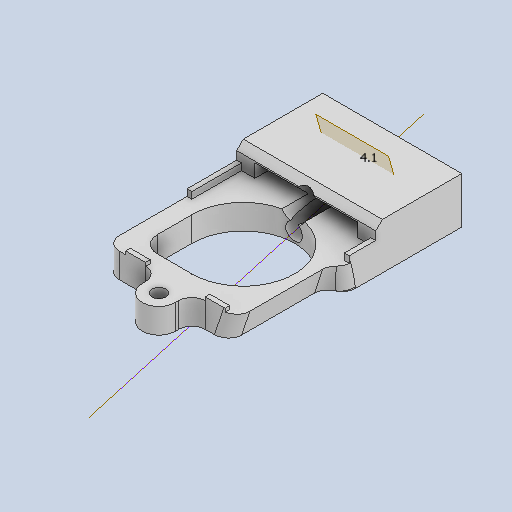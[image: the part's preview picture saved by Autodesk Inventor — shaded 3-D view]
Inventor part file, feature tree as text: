
AUTODESK INVENTOR PART (.ipt)
format: ipt  version: 2023.3 (Build 273359000, 359)  size: 391,168 bytes
history: native  units: mm
features: sketch x15, extrude x9, other x7, hole x5, projected_geometry x5, fillet x3, chamfer x2, plane x2
ambient origin geometry x8: Origin, YZ Plane, XZ Plane, XY Plane, X Axis, Y Axis, Z Axis, Center Point
bodies: Solid1 (feature_tree)
feature tree (48):
  extrude  "Extrusion1"  Depth=14.0mm
  hole  "Hole1"  [1 undecoded]
  extrude  "Extrusion2"  Depth=26.0mm
  hole  "Hole3"  [1 undecoded]
  extrude  "Extrusion3"  Depth=8.0mm TaperAngle=90.0deg
  hole  "Hole2"  [1 undecoded]
  other  "Snap Fit1"
  fillet  "Fillet1"  Radius=2.0mm
  extrude  "Extrusion4"  Depth=8.0mm
  extrude  "Extrusion5"  Depth=2.5mm
  hole  "Hole4"  [1 undecoded]
  fillet  "Fillet2"  Radius=1.0mm
  extrude  "Extrusion6"  Depth=10.0mm
  chamfer  "Chamfer1"  Distance=10.0mm
  chamfer  "Chamfer2"  Distance=4.1mm
  extrude  "Extrusion7"  TaperAngle=45.0deg  [1 undecoded]
  extrude  "Extrusion8"  Depth=10.0mm TaperAngle=0.0deg
  fillet  "Fillet3"  Radius=2.0mm
  sketch  "Sketch15"  dims[d66=18.0mm d68=4.1mm d69=45.0deg d70=31.0mm d71=0.0mm d72=2.0mm d73=2.0mm d74=45.0deg d76=5.0mm d77=6.0mm d78=2.0mm d79=45.0deg d83=15.5mm d84=5.0mm d85=0.0mm d86=0.0mm d87=5.0mm d88=30.0mm d89=0.0mm d90=4.0mm d91=2.5mm d92=45.0deg d93=15.0mm d94=0.0mm d96=1.0mm d97=20.0mm d98=0.0mm d99=4.1mm d100=10.0mm d101=10.0mm d102=5.0mm d103=6.0mm d104=4.0mm d105=2.0mm d106=90.0deg d107=8.0mm d108=0.0mm d67=0.0mm d75=0.5mm d95=0.15mm]
  other  "Work Axis2"
  other  "Work Point1"
  hole  "Hole5"  [1 undecoded]
  plane  "Work Plane1"
  extrude  "Extrusion9"  Depth=10.0mm TaperAngle=45.0deg
  sketch  "Sketch1"  dims[d0=42.0mm d1=14.0mm]
  sketch  "Sketch2"  dims[d2=65.5mm d3=0.0mm d5=9.0mm]
  sketch  "Sketch3"  dims[d6=23.0mm]
  projected_geometry  "Projected Loop1"
  sketch  "Sketch4"  dims[d7=2.95mm d8=6.0mm d9=4.0mm d10=2.0mm d11=90.0deg d12=8.0mm d13=20.594885mm]
  projected_geometry  "Projected Loop2"
  sketch  "Sketch5"  dims[d15=4.6mm d16=6.0mm d17=7.5mm d18=29.0mm d19=90.0deg d20=8.0mm d21=20.594885mm d22=26.0mm]
  projected_geometry  "Projected Loop3"
  sketch  "Sketch6"  dims[d23=4.5mm d24=0.0mm d25=45.0mm]
  sketch  "Sketch7"  dims[d26=31.0mm d27=6.0mm d28=7.5mm d29=60.5mm d30=90.0deg d31=8.0mm d32=20.594885mm]
  sketch  "Sketch8"  dims[d33=1.45mm d34=1.45mm d35=2.0mm d36=0.0mm]
  sketch  "Sketch9"  dims[d37=1.4mm d38=8.0mm]
  sketch  "Sketch10"  dims[d39=5.3mm d40=2.5mm d41=2.9mm d42=2.9mm d43=4.5mm d44=3.0mm d45=1.0mm d46=1.0mm d47=8.726646mm d48=8.726646mm d49=2.9mm]
  sketch  "Sketch11"  dims[d50=6.0mm d51=1.0mm d52=1.0mm d53=0.0mm]
  sketch  "Sketch12"  dims[d54=5.0mm d55=10.0mm d56=10.0mm d57=0.0mm]
  sketch  "Sketch13"  dims[d58=4.2mm d59=6.0mm d60=5.7mm d61=4.2mm d62=90.0deg d63=8.0mm d64=20.594885mm]
  other  "Work Axis1"
  sketch  "Sketch14"  dims[d65=4.0mm]
  projected_geometry  "Projected Loop4"
  projected_geometry  "Projected Loop5"
  plane  "Work Plane2"
  parser-record x1  (decoder bookkeeping rows leaked as tree rows — omitted from the tree; the rows remain in map.json)
  other  "chamber_assembly_3Dprint.iam"
  other  "chamber_V2_new:1"
note: 6 required parameter values undecoded (feature->parameter linkage not recoverable at this tier; creation-order binding heuristic only, values carry confidence <= 0.55)
note: 1 file-system path scrubbed to <path> (originals preserved in map.json)
